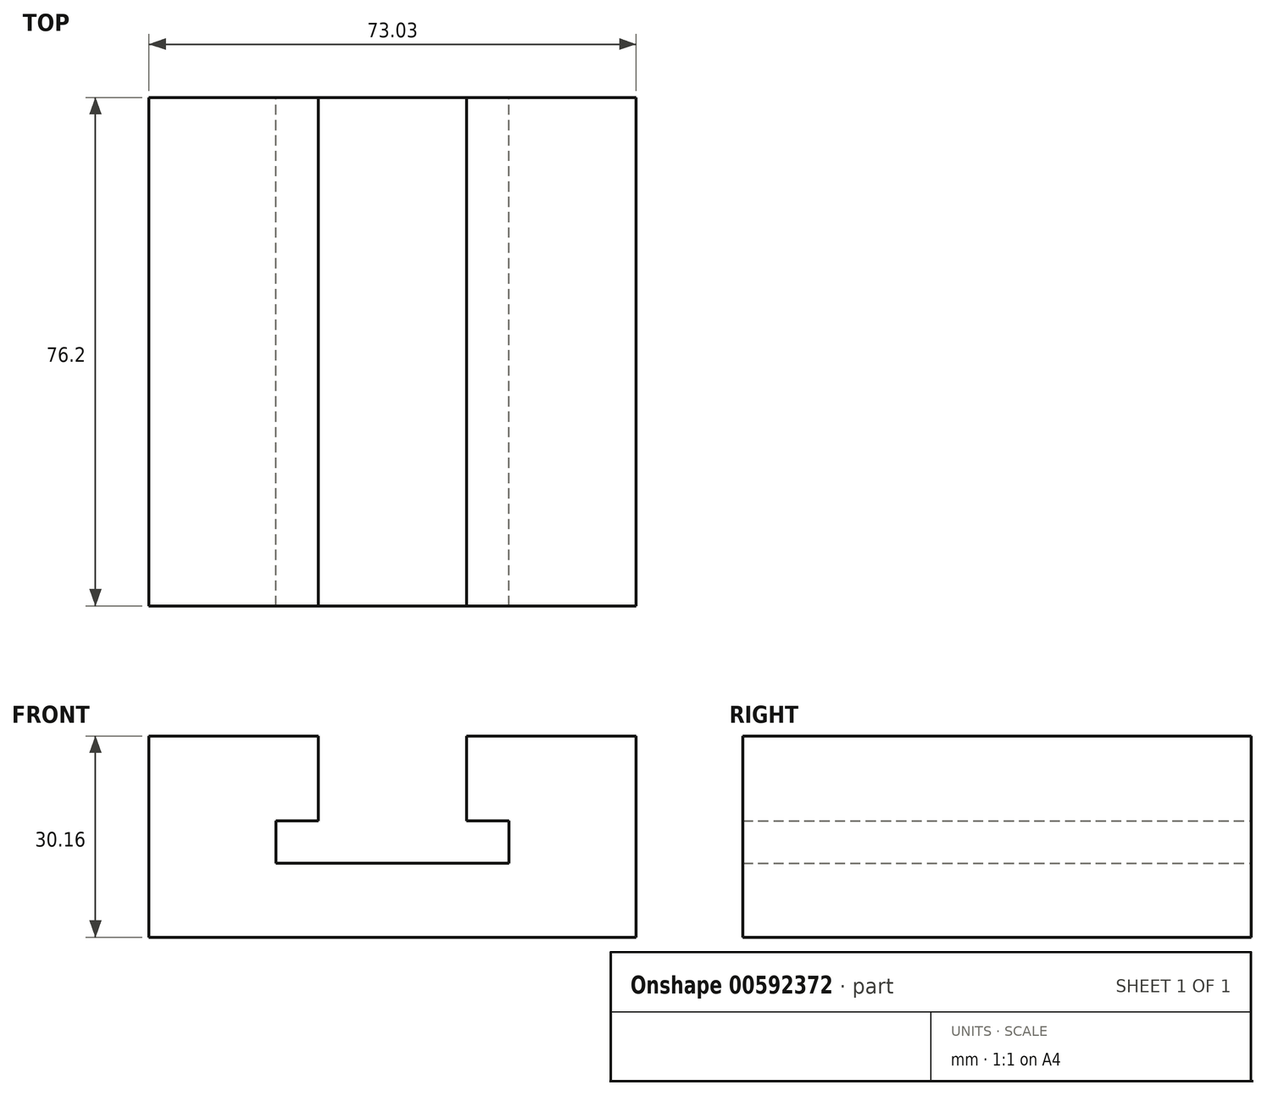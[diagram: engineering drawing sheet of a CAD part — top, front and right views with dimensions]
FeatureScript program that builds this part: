
annotation { "Feature Type Name" : "Feature", "Feature Type Description" : "" }
export const myFeature = defineFeature(function(context is Context, id is Id, definition is map)
    precondition{}
    {
        {
            var Q0;
            Q0=qCreatedBy(makeId("Front.planeOp"),FACE);
            var sketch = newSketch(context, id + "F0", { "sketchPlane" : qUnion([Q0])});
            skLineSegment(sketch, "E0", {"start": v(0, 0) * mm, "end": v(0, 30.16) * mm});
            skLineSegment(sketch, "E1", {"start": v(0, 30.16) * mm, "end": v(25.4, 30.16) * mm});
            skLineSegment(sketch, "E2", {"start": v(25.4, 30.16) * mm, "end": v(25.4, 17.46) * mm});
            skLineSegment(sketch, "E3", {"start": v(25.4, 17.46) * mm, "end": v(19.05, 17.46) * mm});
            skLineSegment(sketch, "E4", {"start": v(19.05, 17.46) * mm, "end": v(19.05, 11.11) * mm});
            skLineSegment(sketch, "E5", {"start": v(19.05, 11.11) * mm, "end": v(53.99, 11.11) * mm});
            skLineSegment(sketch, "E6", {"start": v(53.99, 11.11) * mm, "end": v(53.99, 17.46) * mm});
            skLineSegment(sketch, "E7", {"start": v(53.99, 17.46) * mm, "end": v(47.62, 17.46) * mm});
            skLineSegment(sketch, "E8", {"start": v(47.62, 17.46) * mm, "end": v(47.62, 30.16) * mm});
            skLineSegment(sketch, "E9", {"start": v(47.62, 30.16) * mm, "end": v(73.03, 30.16) * mm});
            skLineSegment(sketch, "E10", {"start": v(73.03, 30.16) * mm, "end": v(73.03, 0) * mm});
            skLineSegment(sketch, "E11", {"start": v(73.03, 0) * mm, "end": v(0, 0) * mm});
            skSolve(sketch);
        }
        {
            var Q0;
            Q0 = qSketchRegion(id + "F0", true);
            extrude(context, id + "F1", {"entities" : qUnion([Q0]), "depth" : 76.2 * mm, "offsetDistance" : 25.4 * mm});
        }
    });
